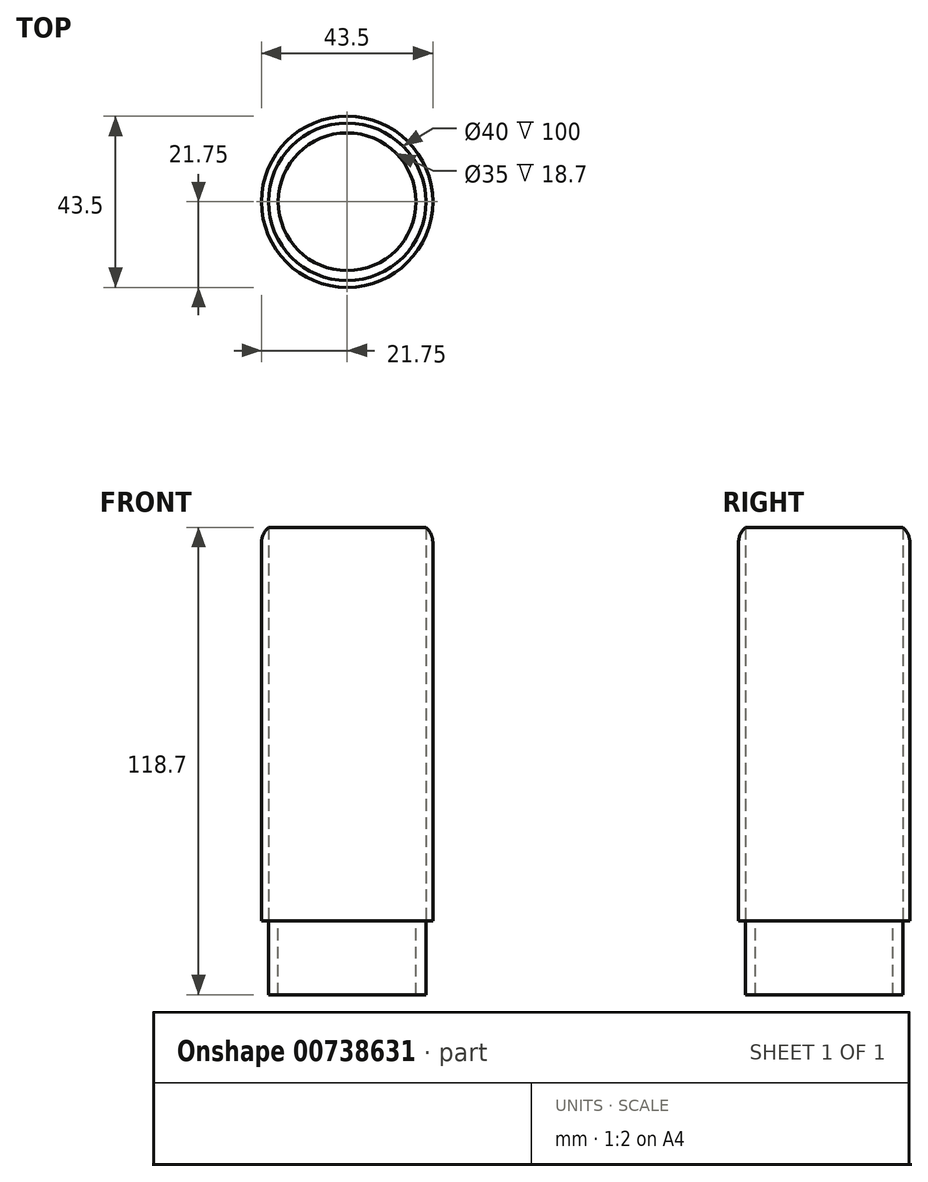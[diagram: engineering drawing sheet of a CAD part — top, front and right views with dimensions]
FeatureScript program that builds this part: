
annotation { "Feature Type Name" : "Feature", "Feature Type Description" : "" }
export const myFeature = defineFeature(function(context is Context, id is Id, definition is map)
    precondition{}
    {
        {
            var Q0;
            Q0=qCreatedBy(makeId("Top.planeOp"),FACE);
            var sketch = newSketch(context, id + "F0", { "sketchPlane" : qUnion([Q0])});
            skCircle(sketch, "E0", {"center": v(0, 0) * mm, "radius": 20 * mm});
            skSolve(sketch);
        }
        {
            var Q0;
            Q0=makeQuery(id+"F0.imprint","IMPRINT",FACE,{"disambiguationData":[TD([[makeQuery(id+"F0.imprint","IMPRINT",EDGE,{"derivedFrom":sQuery(id+"F0.wireOp",EDGE,"E0")}),1.0]])]});
            extrude(context, id + "F1", {"entities" : qUnion([Q0]), "depth" : 18.7 * mm, "offsetDistance" : 25 * mm});
        }
        {
            var Q0;
            Q0=makeQuery(id+"F1.opExtrude","CAP_FACE",FACE,{"disambiguationData":[OSD([sQuery(id+"F0.wireOp",EDGE,"E0")])],"isStart":false});
            var sketch = newSketch(context, id + "F2", { "sketchPlane" : qUnion([Q0])});
            skCircle(sketch, "E1", {"center": v(0, 0) * mm, "radius": 21.75 * mm});
            skSolve(sketch);
        }
        {
            var Q0;
            Q0=makeQuery(id+"F2.imprint","IMPRINT",FACE,{"disambiguationData":[TD([[makeQuery(id+"F2.imprint","IMPRINT",EDGE,{"derivedFrom":sQuery(id+"F2.wireOp",EDGE,"E1")}),1.0]])]});
            extrude(context, id + "F3", {"entities" : qUnion([Q0]), "depth" : 100 * mm, "offsetDistance" : 25 * mm});
        }
        {
            var Q0;
            Q0=makeQuery(id+"F1.opExtrude","CAP_FACE",FACE,{"disambiguationData":[OSD([sQuery(id+"F0.wireOp",EDGE,"E0")])],"isStart":false});
            var sketch = newSketch(context, id + "F4", { "sketchPlane" : qUnion([Q0])});
            skCircle(sketch, "E2", {"center": v(0, 0) * mm, "radius": 17.5 * mm});
            skSolve(sketch);
        }
        {
            var Q0;
            Q0=makeQuery(id+"F4.imprint","IMPRINT",FACE,{"disambiguationData":[TD([[makeQuery(id+"F4.imprint","IMPRINT",EDGE,{"derivedFrom":sQuery(id+"F4.wireOp",EDGE,"E2")}),1.0]])]});
            extrude(context, id + "F5", {"entities" : qUnion([Q0]), "operationType" : NewBodyOperationType.REMOVE, "oppositeDirection" : true, "depth" : 25 * mm, "offsetDistance" : 25 * mm});
        }
        {
            var Q0;
            Q0=makeQuery(id+"F3.opExtrude","CAP_EDGE",EDGE,{"disambiguationData":[OSD([sQuery(id+"F2.wireOp",EDGE,"E1")])],"isStart":false});
            fillet(context, id + "F6", {"entities" : qUnion([Q0]), "radius" : 5 * mm, "tangentPropagation" : true, "allowEdgeOverflow" : false});
        }
    });
